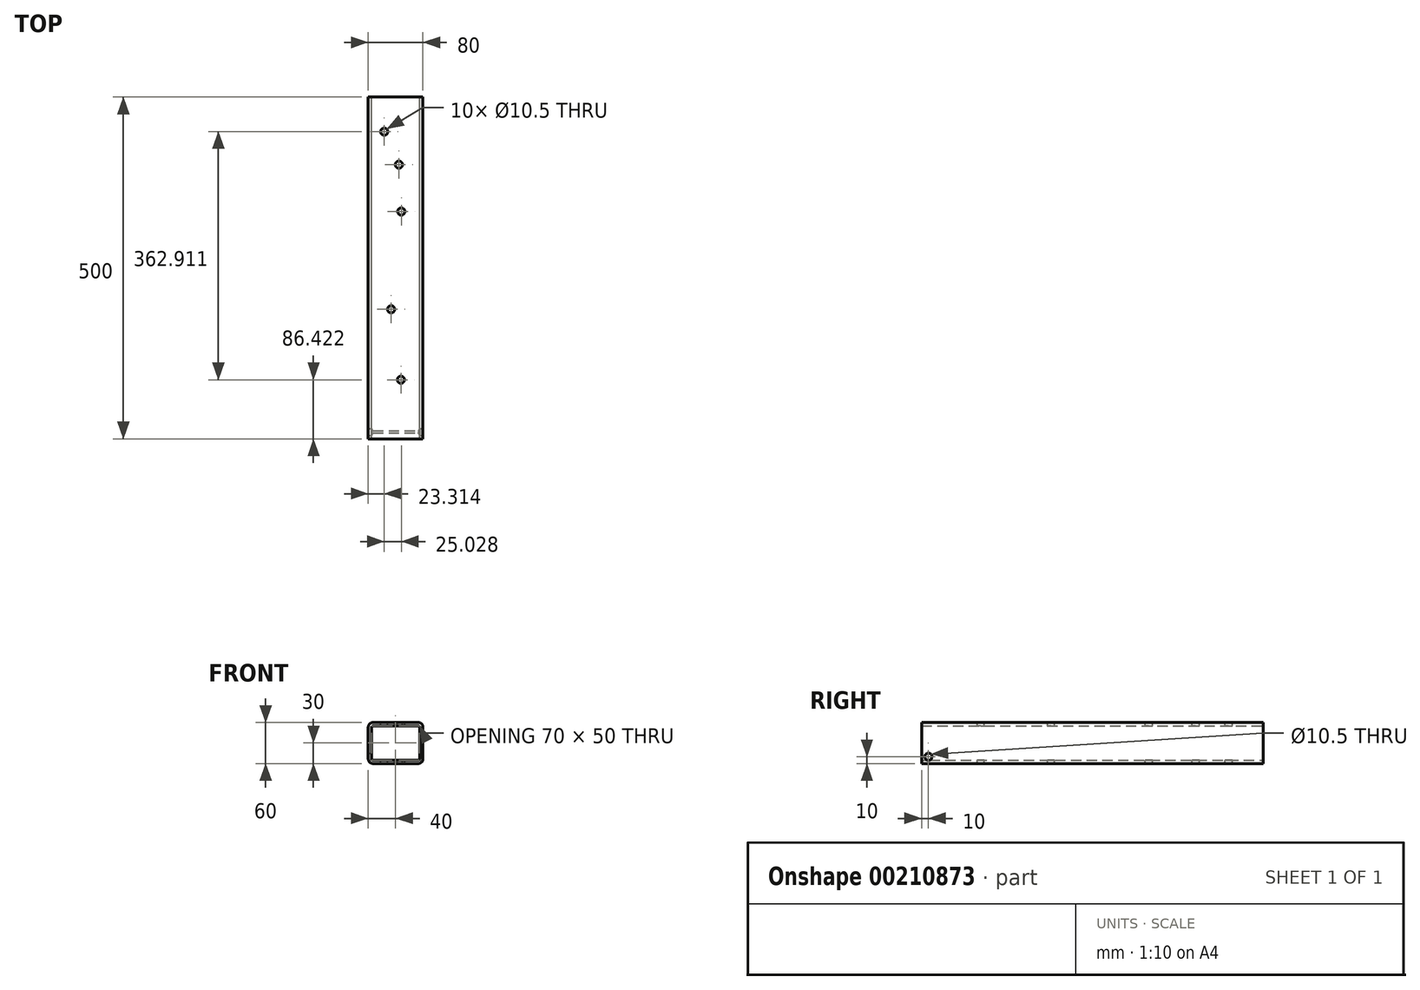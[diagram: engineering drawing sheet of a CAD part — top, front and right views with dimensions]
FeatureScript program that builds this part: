
annotation { "Feature Type Name" : "Feature", "Feature Type Description" : "" }
export const myFeature = defineFeature(function(context is Context, id is Id, definition is map)
    precondition{}
    {
        {
            var Q0;
            Q0=qCreatedBy(makeId("Front.planeOp"),FACE);
            var sketch = newSketch(context, id + "F0", { "sketchPlane" : qUnion([Q0])});
            skLineSegment(sketch, "E0.bottom", {"start": v(33, 30) * mm, "end": v(-33, 30) * mm});
            skLineSegment(sketch, "E0.top", {"start": v(33, -30) * mm, "end": v(-33, -30) * mm});
            skLineSegment(sketch, "E0.left", {"start": v(40, 23) * mm, "end": v(40, -23) * mm});
            skLineSegment(sketch, "E0.right", {"start": v(-40, 23) * mm, "end": v(-40, -23) * mm});
            skPoint(sketch, "E0.middle", {"position": v(0, 0) * mm});
            skLineSegment(sketch, "E1.bottom", {"start": v(33, 25) * mm, "end": v(-33, 25) * mm});
            skLineSegment(sketch, "E1.top", {"start": v(33, -25) * mm, "end": v(-33, -25) * mm});
            skLineSegment(sketch, "E1.left", {"start": v(35, 23) * mm, "end": v(35, -23) * mm});
            skLineSegment(sketch, "E1.right", {"start": v(-35, 23) * mm, "end": v(-35, -23) * mm});
            skPoint(sketch, "E2.visualSharp", {"position": v(-40, 30) * mm});
            skArc(sketch, "E2.filletArc", {"start": v(-33, 30) * mm, "mid": v(-37.95, 27.95) * mm, "end": v(-40, 23) * mm});
            skPoint(sketch, "E3.visualSharp", {"position": v(-40, -30) * mm});
            skArc(sketch, "E3.filletArc", {"start": v(-40, -23) * mm, "mid": v(-37.95, -27.95) * mm, "end": v(-33, -30) * mm});
            skPoint(sketch, "E4.visualSharp", {"position": v(40, -30) * mm});
            skArc(sketch, "E4.filletArc", {"start": v(33, -30) * mm, "mid": v(37.95, -27.95) * mm, "end": v(40, -23) * mm});
            skPoint(sketch, "E5.visualSharp", {"position": v(40, 30) * mm});
            skArc(sketch, "E5.filletArc", {"start": v(40, 23) * mm, "mid": v(37.95, 27.95) * mm, "end": v(33, 30) * mm});
            skPoint(sketch, "E6.visualSharp", {"position": v(-35, -25) * mm});
            skArc(sketch, "E6.filletArc", {"start": v(-35, -23) * mm, "mid": v(-34.41, -24.41) * mm, "end": v(-33, -25) * mm});
            skPoint(sketch, "E7.visualSharp", {"position": v(35, 25) * mm});
            skArc(sketch, "E7.filletArc", {"start": v(35, 23) * mm, "mid": v(34.41, 24.41) * mm, "end": v(33, 25) * mm});
            skPoint(sketch, "E8.visualSharp", {"position": v(35, -25) * mm});
            skArc(sketch, "E8.filletArc", {"start": v(33, -25) * mm, "mid": v(34.41, -24.41) * mm, "end": v(35, -23) * mm});
            skPoint(sketch, "E9.visualSharp", {"position": v(-35, 25) * mm});
            skArc(sketch, "E9.filletArc", {"start": v(-33, 25) * mm, "mid": v(-34.41, 24.41) * mm, "end": v(-35, 23) * mm});
            skSolve(sketch);
        }
        {
            var Q0;
            Q0=makeQuery(id+"F0.imprint","IMPRINT",FACE,{"disambiguationData":[TD([[makeQuery(id+"F0.imprint","IMPRINT",EDGE,{"derivedFrom":sQuery(id+"F0.wireOp",EDGE,"E0.bottom")}),1.0]])]});
            extrude(context, id + "F1", {"entities" : qUnion([Q0]), "endBound" : BoundingType.SYMMETRIC, "depth" : 500 * mm});
        }
        {
            var Q0;
            Q0=makeQuery(id+"F1.opExtrude","SWEPT_FACE",FACE,{"disambiguationData":[OSD([sQuery(id+"F0.wireOp",EDGE,"E0.right")])]});
            var sketch = newSketch(context, id + "F2", { "sketchPlane" : qUnion([Q0])});
            skLineSegment(sketch, "E10.0", {"start": v(-190, -30) * mm, "end": v(-250, -30) * mm});
            skPoint(sketch, "E11.0", {"position": v(-250, 30) * mm});
            skLineSegment(sketch, "E12", {"start": v(-250, 30) * mm, "end": v(-250, -30) * mm});
            skLineSegment(sketch, "E13", {"start": v(-250, 30) * mm, "end": v(-190, -30) * mm});
            skPoint(sketch, "E14.orphan", {"position": v(250, -30) * mm});
            skLineSegment(sketch, "E15.MirrorCS", {"start": v(250, 30) * mm, "end": v(250, -30) * mm});
            skLineSegment(sketch, "E16.MirrorCS", {"start": v(250, 30) * mm, "end": v(190, -30) * mm});
            skLineSegment(sketch, "E17.MirrorCS", {"start": v(190, -30) * mm, "end": v(250, -30) * mm});
            skSolve(sketch);
        }
        {
            var Q0;
            Q0=makeQuery(id+"F1.opExtrude","SWEPT_FACE",FACE,{"disambiguationData":[OSD([sQuery(id+"F0.wireOp",EDGE,"E0.bottom")])]});
            var sketch = newSketch(context, id + "F3", { "sketchPlane" : qUnion([Q0])});
            skPoint(sketch, "E18", {"position": v(-16.69, 199.33) * mm});
            skPoint(sketch, "E19", {"position": v(4.77, 151.06) * mm});
            skPoint(sketch, "E20", {"position": v(8.34, 82.53) * mm});
            skPoint(sketch, "E21", {"position": v(-6.56, -60.49) * mm});
            skPoint(sketch, "E22", {"position": v(7.75, -163.58) * mm});
            skSolve(sketch);
        }
        {
            var Q0;
            Q0=sQuery(id+"F3.wireOp",VERTEX,"E22");
            var Q1;
            Q1=sQuery(id+"F3.wireOp",VERTEX,"E21");
            var Q2;
            Q2=sQuery(id+"F3.wireOp",VERTEX,"E20");
            var Q3;
            Q3=sQuery(id+"F3.wireOp",VERTEX,"E19");
            var Q4;
            Q4=sQuery(id+"F3.wireOp",VERTEX,"E18");
            var Q5;
            Q5=makeQuery(id+"F1.opExtrude","SWEPT_BODY",BODY,{"disambiguationData":[OSD([sQuery(id+"F0.wireOp",EDGE,"E0.bottom"),sQuery(id+"F0.wireOp",EDGE,"E0.top"),sQuery(id+"F0.wireOp",EDGE,"E0.left"),sQuery(id+"F0.wireOp",EDGE,"E0.right"),sQuery(id+"F0.wireOp",EDGE,"E1.bottom"),sQuery(id+"F0.wireOp",EDGE,"E1.top"),sQuery(id+"F0.wireOp",EDGE,"E1.left"),sQuery(id+"F0.wireOp",EDGE,"E1.right"),sQuery(id+"F0.wireOp",EDGE,"E2.filletArc"),sQuery(id+"F0.wireOp",EDGE,"E3.filletArc"),sQuery(id+"F0.wireOp",EDGE,"E4.filletArc"),sQuery(id+"F0.wireOp",EDGE,"E5.filletArc"),sQuery(id+"F0.wireOp",EDGE,"E6.filletArc"),sQuery(id+"F0.wireOp",EDGE,"E7.filletArc"),sQuery(id+"F0.wireOp",EDGE,"E8.filletArc"),sQuery(id+"F0.wireOp",EDGE,"E9.filletArc")])]});
            hole(context, id + "F4", {"style" : HoleStyle.SIMPLE, "endStyle" : HoleEndStyle.THROUGH, "standardTappedOrClearance" : lookupTablePath({ "standard" : "ISO", "engagement" : "75%", "pitch" : "1.5 mm", "size" : "M12", "type" : "Tapped" }), "standardBlindInLast" : lookupTablePath({ "standard" : "ISO", "engagement" : "75%", "pitch" : "1.5 mm", "size" : "M12", "type" : "Tapped" }), "holeDiameter" : 10.5 * mm, "locations" : qUnion([Q0, Q1, Q2, Q3, Q4]), "scope" : qUnion([Q5]), "isTappedThrough" : true, "majorDiameter" : 12 * mm, "showTappedDepth" : true});
        }
        {
            var Q0;
            Q0=makeQuery(id+"F1.opExtrude","SWEPT_FACE",FACE,{"disambiguationData":[OSD([sQuery(id+"F0.wireOp",EDGE,"E0.left")])]});
            var sketch = newSketch(context, id + "F5", { "sketchPlane" : qUnion([Q0])});
            skPoint(sketch, "E23", {"position": v(-240, -20) * mm});
            skSolve(sketch);
        }
        {
            var Q0;
            Q0=sQuery(id+"F5.wireOp",VERTEX,"E23");
            var Q1;
            Q1=makeQuery(id+"F1.opExtrude","SWEPT_BODY",BODY,{"disambiguationData":[OSD([sQuery(id+"F0.wireOp",EDGE,"E0.bottom"),sQuery(id+"F0.wireOp",EDGE,"E0.top"),sQuery(id+"F0.wireOp",EDGE,"E0.left"),sQuery(id+"F0.wireOp",EDGE,"E0.right"),sQuery(id+"F0.wireOp",EDGE,"E1.bottom"),sQuery(id+"F0.wireOp",EDGE,"E1.top"),sQuery(id+"F0.wireOp",EDGE,"E1.left"),sQuery(id+"F0.wireOp",EDGE,"E1.right"),sQuery(id+"F0.wireOp",EDGE,"E2.filletArc"),sQuery(id+"F0.wireOp",EDGE,"E3.filletArc"),sQuery(id+"F0.wireOp",EDGE,"E4.filletArc"),sQuery(id+"F0.wireOp",EDGE,"E5.filletArc"),sQuery(id+"F0.wireOp",EDGE,"E6.filletArc"),sQuery(id+"F0.wireOp",EDGE,"E7.filletArc"),sQuery(id+"F0.wireOp",EDGE,"E8.filletArc"),sQuery(id+"F0.wireOp",EDGE,"E9.filletArc")])]});
            hole(context, id + "F6", {"style" : HoleStyle.SIMPLE, "endStyle" : HoleEndStyle.THROUGH, "standardTappedOrClearance" : lookupTablePath({ "standard" : "ISO", "engagement" : "75%", "pitch" : "1.5 mm", "size" : "M12", "type" : "Tapped" }), "standardBlindInLast" : lookupTablePath({ "standard" : "ISO", "engagement" : "75%", "pitch" : "1.5 mm", "size" : "M12", "type" : "Tapped" }), "holeDiameter" : 10.5 * mm, "locations" : qUnion([Q0]), "scope" : qUnion([Q1]), "isTappedThrough" : true, "majorDiameter" : 12 * mm, "showTappedDepth" : true});
        }
    });
